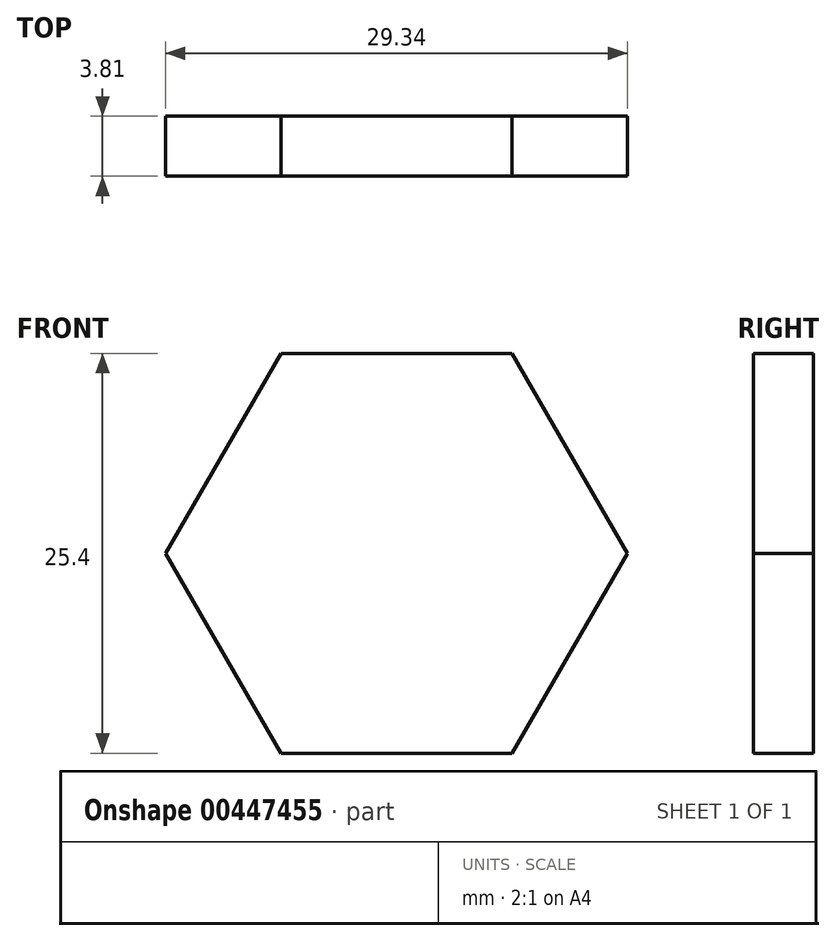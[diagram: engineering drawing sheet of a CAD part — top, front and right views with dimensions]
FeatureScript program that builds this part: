
annotation { "Feature Type Name" : "Feature", "Feature Type Description" : "" }
export const myFeature = defineFeature(function(context is Context, id is Id, definition is map)
    precondition{}
    {
        {
            var Q0;
            Q0=qCreatedBy(makeId("Front.planeOp"),FACE);
            var sketch = newSketch(context, id + "F0", { "sketchPlane" : qUnion([Q0])});
            skLineSegment(sketch, "E0.bottom", {"start": v(7.33, -12.7) * mm, "end": v(-7.33, -12.7) * mm});
            skLineSegment(sketch, "E0.top", {"start": v(7.33, 12.7) * mm, "end": v(-7.33, 12.7) * mm});
            skPoint(sketch, "E1.middle", {"position": v(0, 0) * mm});
            skLineSegment(sketch, "E2", {"start": v(-7.33, 12.7) * mm, "end": v(-14.67, 0) * mm});
            skLineSegment(sketch, "E3", {"start": v(-14.67, 0) * mm, "end": v(-7.33, -12.7) * mm});
            skLineSegment(sketch, "E4", {"start": v(7.33, -12.7) * mm, "end": v(14.67, 0) * mm});
            skLineSegment(sketch, "E5", {"start": v(14.67, 0) * mm, "end": v(7.33, 12.7) * mm});
            skSolve(sketch);
        }
        {
            var Q0;
            Q0=makeQuery(id+"F0.imprint","IMPRINT",FACE,{"disambiguationData":[TD([[makeQuery(id+"F0.imprint","IMPRINT",EDGE,{"derivedFrom":sQuery(id+"F0.wireOp",EDGE,"E0.bottom")}),-1.0]])]});
            extrude(context, id + "F1", {"entities" : qUnion([Q0]), "depth" : 3.8 * mm});
        }
    });
